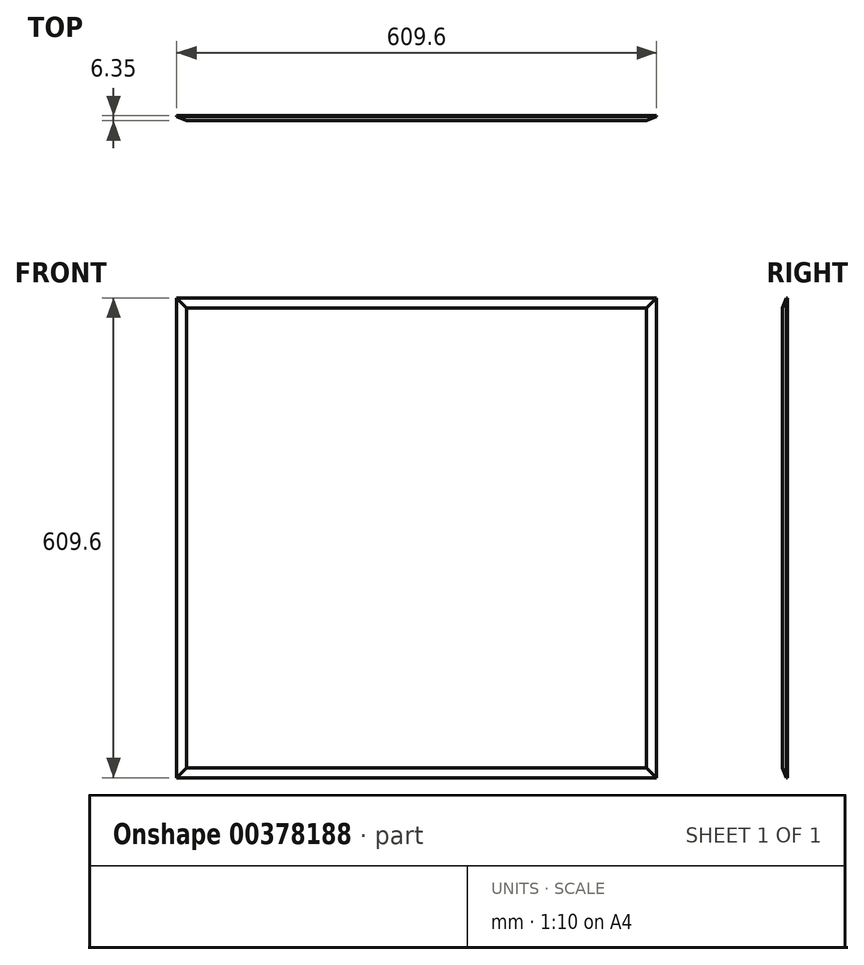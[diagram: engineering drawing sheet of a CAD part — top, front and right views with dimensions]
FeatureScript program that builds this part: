
annotation { "Feature Type Name" : "Feature", "Feature Type Description" : "" }
export const myFeature = defineFeature(function(context is Context, id is Id, definition is map)
    precondition{}
    {
        {
            var Q0;
            Q0=qCreatedBy(makeId("Front.planeOp"),FACE);
            var sketch = newSketch(context, id + "F0", { "sketchPlane" : qUnion([Q0])});
            skLineSegment(sketch, "E0.bottom", {"start": v(304.8, 304.8) * mm, "end": v(-304.8, 304.8) * mm});
            skLineSegment(sketch, "E0.top", {"start": v(304.8, -304.8) * mm, "end": v(-304.8, -304.8) * mm});
            skLineSegment(sketch, "E0.left", {"start": v(304.8, 304.8) * mm, "end": v(304.8, -304.8) * mm});
            skLineSegment(sketch, "E0.right", {"start": v(-304.8, 304.8) * mm, "end": v(-304.8, -304.8) * mm});
            skPoint(sketch, "E0.middle", {"position": v(0, 0) * mm});
            skSolve(sketch);
        }
        {
            var Q0;
            Q0=makeQuery(id+"F0.imprint","IMPRINT",FACE,{"disambiguationData":[TD([[makeQuery(id+"F0.imprint","IMPRINT",EDGE,{"derivedFrom":sQuery(id+"F0.wireOp",EDGE,"E0.bottom")}),1.0]])]});
            extrude(context, id + "F1", {"entities" : qUnion([Q0]), "depth" : 6.35 * mm});
        }
        {
            var Q0;
            Q0=makeQuery(id+"F1.opExtrude","CAP_FACE",FACE,{"disambiguationData":[OSD([sQuery(id+"F0.wireOp",EDGE,"E0.bottom"),sQuery(id+"F0.wireOp",EDGE,"E0.top"),sQuery(id+"F0.wireOp",EDGE,"E0.left"),sQuery(id+"F0.wireOp",EDGE,"E0.right")])],"isStart":false});
            chamfer(context, id + "F2", {"entities" : qUnion([Q0]), "chamferType" : ChamferType.TWO_OFFSETS, "width1" : 12.7 * mm, "oppositeDirection" : false, "width2" : 5.08 * mm, "tangentPropagation" : true});
        }
    });
